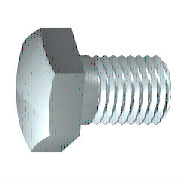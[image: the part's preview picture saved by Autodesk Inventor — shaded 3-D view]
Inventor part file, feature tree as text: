
AUTODESK INVENTOR PART (.ipt)
format: ipt  version: 2024.2 (Build 282272000, 272)  size: 188,928 bytes
history: native  units: mm (DEFAULTED — no unit token found)
features: extrude x1, chamfer x1, plane x1
ambient origin geometry x7: Origin, YZ Plane, XZ Plane, X Axis, Y Axis, Z Axis, Center Point
bodies: Solid1 (feature_tree), Body (feature_tree)
feature tree (3):
  extrude  "Head"  Depth=100.0mm
  chamfer  "Chamfer1"  Distance=94.7mm
  plane  "Work Plane1"
